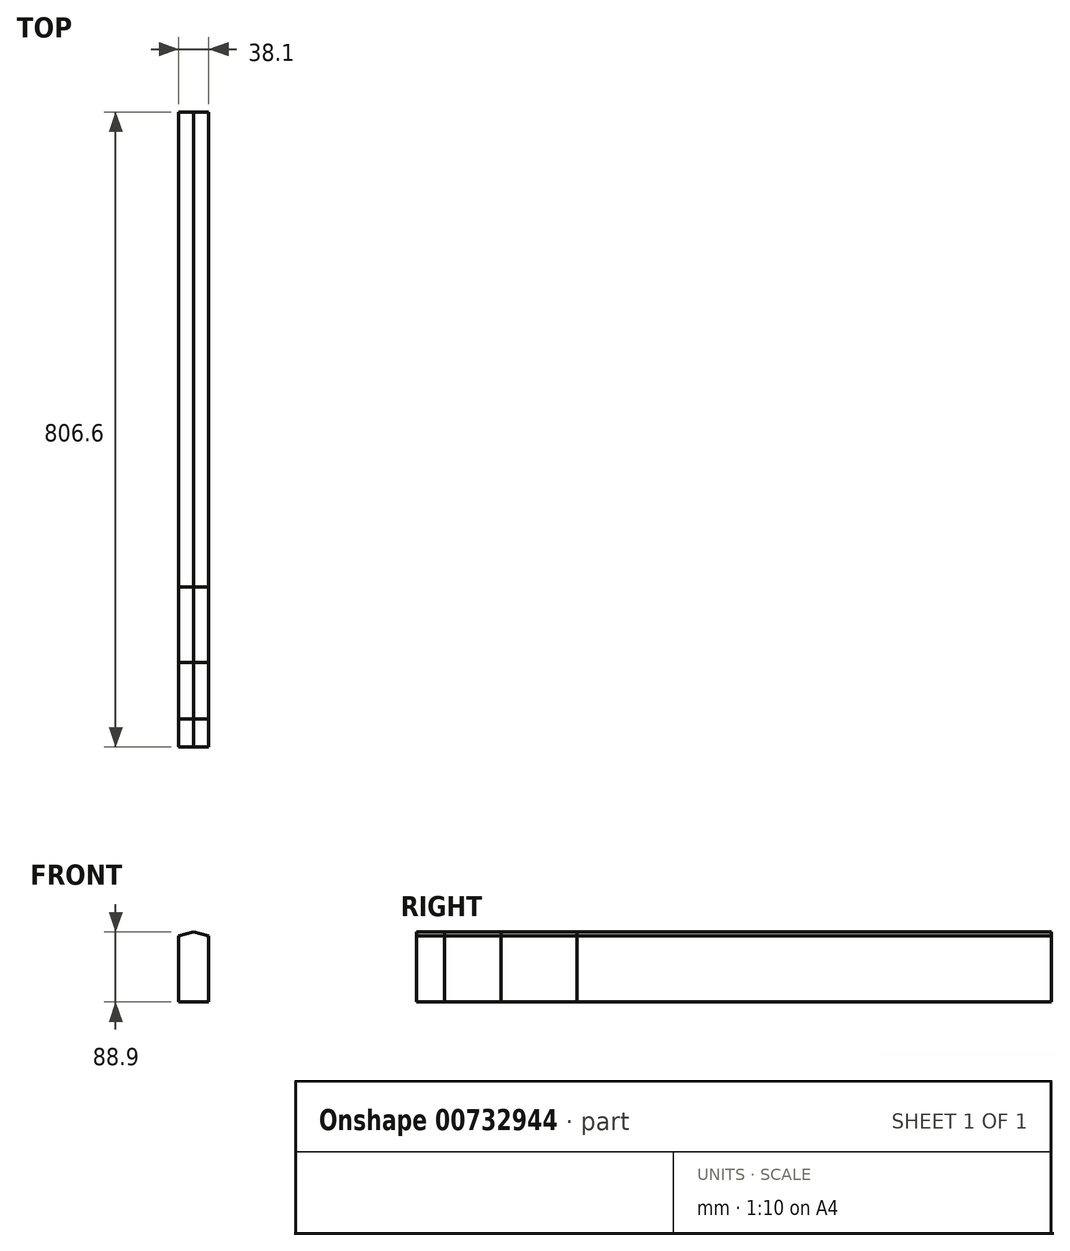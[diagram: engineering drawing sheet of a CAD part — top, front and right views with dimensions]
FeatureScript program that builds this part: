
annotation { "Feature Type Name" : "Feature", "Feature Type Description" : "" }
export const myFeature = defineFeature(function(context is Context, id is Id, definition is map)
    precondition{}
    {
        {
            var Q0;
            Q0=qCreatedBy(makeId("Front.planeOp"),FACE);
            var sketch = newSketch(context, id + "F0", { "sketchPlane" : qUnion([Q0])});
            skLineSegment(sketch, "E0", {"start": v(0, 0) * mm, "end": v(-19.05, -5.1) * mm});
            skLineSegment(sketch, "E1", {"start": v(-19.05, -5.1) * mm, "end": v(-19.05, -88.9) * mm});
            skLineSegment(sketch, "E2", {"start": v(-19.05, -88.9) * mm, "end": v(19.05, -88.9) * mm});
            skLineSegment(sketch, "E3", {"start": v(19.05, -88.9) * mm, "end": v(19.05, -5.1) * mm});
            skLineSegment(sketch, "E4", {"start": v(19.05, -5.1) * mm, "end": v(0, 0) * mm});
            skSolve(sketch);
        }
        {
            var Q0;
            Q0 = qSketchRegion(id + "F0", true);
            extrude(context, id + "F1", {"entities" : qUnion([Q0]), "depth" : 602.97 * mm, "offsetDistance" : 25.4 * mm});
        }
        {
            var Q0;
            Q0 = qSketchRegion(id + "F0", true);
            extrude(context, id + "F2", {"entities" : qUnion([Q0]), "depth" : 699.13 * mm, "offsetDistance" : 25.4 * mm});
        }
        {
            var Q0;
            Q0 = qSketchRegion(id + "F0", true);
            extrude(context, id + "F3", {"entities" : qUnion([Q0]), "depth" : 770.8 * mm, "offsetDistance" : 25.4 * mm});
        }
        {
            var Q0;
            Q0 = qSketchRegion(id + "F0", true);
            extrude(context, id + "F4", {"entities" : qUnion([Q0]), "depth" : 806.6 * mm, "offsetDistance" : 25.4 * mm});
        }
    });
